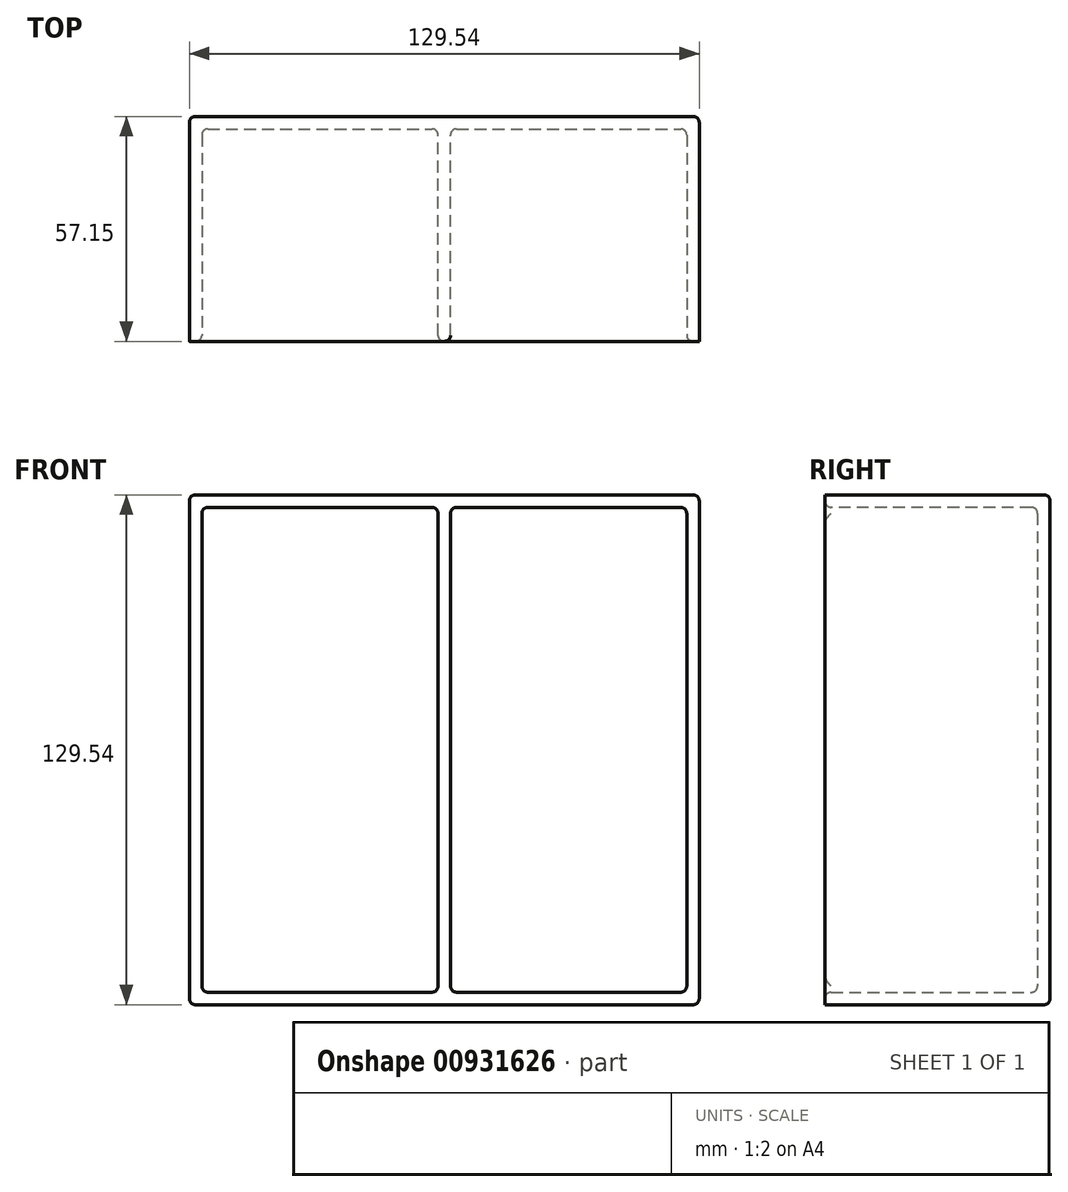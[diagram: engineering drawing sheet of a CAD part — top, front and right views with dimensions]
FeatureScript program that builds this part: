
annotation { "Feature Type Name" : "Feature", "Feature Type Description" : "" }
export const myFeature = defineFeature(function(context is Context, id is Id, definition is map)
    precondition{}
    {
        {
            var Q0;
            Q0=qCreatedBy(makeId("Front.planeOp"),FACE);
            var sketch = newSketch(context, id + "F0", { "sketchPlane" : qUnion([Q0])});
            skLineSegment(sketch, "E0.bottom", {"start": v(0, 0) * mm, "end": v(129.54, 0) * mm});
            skLineSegment(sketch, "E0.top", {"start": v(0, 129.54) * mm, "end": v(129.54, 129.54) * mm});
            skLineSegment(sketch, "E0.left", {"start": v(0, 0) * mm, "end": v(0, 129.54) * mm});
            skLineSegment(sketch, "E0.right", {"start": v(129.54, 0) * mm, "end": v(129.54, 129.54) * mm});
            skSolve(sketch);
        }
        {
            var Q0;
            Q0=makeQuery(id+"F0.imprint","IMPRINT",FACE,{"disambiguationData":[TD([[makeQuery(id+"F0.imprint","IMPRINT",EDGE,{"derivedFrom":sQuery(id+"F0.wireOp",EDGE,"E0.bottom")}),1.0]])]});
            extrude(context, id + "F1", {"entities" : qUnion([Q0]), "oppositeDirection" : true, "depth" : 57.15 * mm, "offsetDistance" : 25.4 * mm});
        }
        {
            var Q0;
            Q0=makeQuery(id+"F1.opExtrude","CAP_FACE",FACE,{"disambiguationData":[OSD([sQuery(id+"F0.wireOp",EDGE,"E0.bottom"),sQuery(id+"F0.wireOp",EDGE,"E0.top"),sQuery(id+"F0.wireOp",EDGE,"E0.left"),sQuery(id+"F0.wireOp",EDGE,"E0.right")])],"isStart":true});
            shell(context, id + "F2", {"entities" : qUnion([Q0]), "thickness" : 3.17 * mm});
        }
        {
            var Q0;
            Q0=makeQuery(id+"F2.opShell","OFFSET_EDGE",EDGE,{"disambiguationData":[OSD([sQuery(id+"F0.wireOp",EDGE,"E0.top"),sQuery(id+"F0.wireOp",EDGE,"E0.left")])]});
            var Q1;
            {var subQ0=sQuery(id+"F0.wireOp",EDGE,"E0.top");Q1=makeQuery(id+"F2.opShell","OFFSET_EDGE",EDGE,{"disambiguationData":[OSD([subQ0]),TDD([makeQuery(id+"F1.opExtrude","CAP_EDGE",EDGE,{"disambiguationData":[OSD([subQ0])],"isStart":false})])]});}
            var Q2;
            {var subQ0=sQuery(id+"F0.wireOp",EDGE,"E0.left");Q2=makeQuery(id+"F2.opShell","OFFSET_EDGE",EDGE,{"disambiguationData":[OSD([subQ0]),TDD([makeQuery(id+"F1.opExtrude","CAP_EDGE",EDGE,{"disambiguationData":[OSD([subQ0])],"isStart":false})])]});}
            var Q3;
            Q3=makeQuery(id+"F2.opShell","OFFSET_EDGE",EDGE,{"disambiguationData":[OSD([sQuery(id+"F0.wireOp",EDGE,"E0.bottom"),sQuery(id+"F0.wireOp",EDGE,"E0.left")])]});
            var Q4;
            {var subQ0=sQuery(id+"F0.wireOp",EDGE,"E0.bottom");Q4=makeQuery(id+"F2.opShell","OFFSET_EDGE",EDGE,{"disambiguationData":[OSD([subQ0]),TDD([makeQuery(id+"F1.opExtrude","CAP_EDGE",EDGE,{"disambiguationData":[OSD([subQ0])],"isStart":false})])]});}
            var Q5;
            {var subQ0=sQuery(id+"F0.wireOp",EDGE,"E0.right");Q5=makeQuery(id+"F2.opShell","OFFSET_EDGE",EDGE,{"disambiguationData":[OSD([subQ0]),TDD([makeQuery(id+"F1.opExtrude","CAP_EDGE",EDGE,{"disambiguationData":[OSD([subQ0])],"isStart":false})])]});}
            var Q6;
            Q6=makeQuery(id+"F2.opShell","OFFSET_EDGE",EDGE,{"disambiguationData":[OSD([sQuery(id+"F0.wireOp",EDGE,"E0.top"),sQuery(id+"F0.wireOp",EDGE,"E0.right")])]});
            var Q7;
            Q7=makeQuery(id+"F2.opShell","OFFSET_EDGE",EDGE,{"disambiguationData":[OSD([sQuery(id+"F0.wireOp",EDGE,"E0.bottom"),sQuery(id+"F0.wireOp",EDGE,"E0.right")])]});
            fillet(context, id + "F3", {"entities" : qUnion([Q0, Q1, Q2, Q3, Q4, Q5, Q6, Q7]), "radius" : 1.52 * mm, "tangentPropagation" : true, "allowEdgeOverflow" : false});
        }
        {
            var Q0;
            Q0=makeQuery(id+"F1.opExtrude","SWEPT_EDGE",EDGE,{"disambiguationData":[OSD([sQuery(id+"F0.wireOp",EDGE,"E0.bottom"),sQuery(id+"F0.wireOp",EDGE,"E0.right")])]});
            var Q1;
            Q1=makeQuery(id+"F1.opExtrude","CAP_EDGE",EDGE,{"disambiguationData":[OSD([sQuery(id+"F0.wireOp",EDGE,"E0.bottom")])],"isStart":false});
            var Q2;
            Q2=makeQuery(id+"F1.opExtrude","CAP_EDGE",EDGE,{"disambiguationData":[OSD([sQuery(id+"F0.wireOp",EDGE,"E0.right")])],"isStart":false});
            var Q3;
            Q3=makeQuery(id+"F1.opExtrude","SWEPT_EDGE",EDGE,{"disambiguationData":[OSD([sQuery(id+"F0.wireOp",EDGE,"E0.top"),sQuery(id+"F0.wireOp",EDGE,"E0.right")])]});
            var Q4;
            Q4=makeQuery(id+"F1.opExtrude","CAP_EDGE",EDGE,{"disambiguationData":[OSD([sQuery(id+"F0.wireOp",EDGE,"E0.top")])],"isStart":false});
            var Q5;
            Q5=makeQuery(id+"F1.opExtrude","SWEPT_EDGE",EDGE,{"disambiguationData":[OSD([sQuery(id+"F0.wireOp",EDGE,"E0.top"),sQuery(id+"F0.wireOp",EDGE,"E0.left")])]});
            var Q6;
            Q6=makeQuery(id+"F1.opExtrude","CAP_EDGE",EDGE,{"disambiguationData":[OSD([sQuery(id+"F0.wireOp",EDGE,"E0.left")])],"isStart":false});
            var Q7;
            Q7=makeQuery(id+"F1.opExtrude","SWEPT_EDGE",EDGE,{"disambiguationData":[OSD([sQuery(id+"F0.wireOp",EDGE,"E0.bottom"),sQuery(id+"F0.wireOp",EDGE,"E0.left")])]});
            fillet(context, id + "F4", {"entities" : qUnion([Q0, Q1, Q2, Q3, Q4, Q5, Q6, Q7]), "radius" : 1.52 * mm, "tangentPropagation" : true, "allowEdgeOverflow" : false});
        }
        {
            var Q0;
            Q0=makeQuery(id+"F2.opShell","OFFSET_FACE",FACE,{"disambiguationData":[OSD([sQuery(id+"F0.wireOp",EDGE,"E0.bottom"),sQuery(id+"F0.wireOp",EDGE,"E0.top"),sQuery(id+"F0.wireOp",EDGE,"E0.left"),sQuery(id+"F0.wireOp",EDGE,"E0.right")])]});
            var sketch = newSketch(context, id + "F5", { "sketchPlane" : qUnion([Q0])});
            skLineSegment(sketch, "E1.0", {"start": v(63.18, 126.37) * mm, "end": v(63.18, 3.17) * mm});
            skLineSegment(sketch, "E2.0", {"start": v(66.36, 126.37) * mm, "end": v(66.36, 3.17) * mm});
            skPoint(sketch, "E3.end.orphan", {"position": v(64.77, 3.17) * mm});
            skPoint(sketch, "E3.start.orphan", {"position": v(64.77, 126.37) * mm});
            skLineSegment(sketch, "E4", {"start": v(63.18, 126.37) * mm, "end": v(66.36, 126.37) * mm});
            skLineSegment(sketch, "E5", {"start": v(66.36, 3.17) * mm, "end": v(63.18, 3.17) * mm});
            skSolve(sketch);
        }
        {
            var Q0;
            Q0=makeQuery(id+"F5.imprint","IMPRINT",FACE,{"disambiguationData":[TD([[makeQuery(id+"F5.imprint","IMPRINT",EDGE,{"derivedFrom":sQuery(id+"F5.wireOp",EDGE,"E1.0")}),1.0]])]});
            extrude(context, id + "F6", {"entities" : qUnion([Q0]), "operationType" : NewBodyOperationType.ADD, "depth" : 53.97 * mm, "offsetDistance" : 25.4 * mm});
        }
        {
            var Q0;
            {var subQ1=sQuery(id+"F0.wireOp",EDGE,"E0.top");var subQ2=sQuery(id+"F5.wireOp",EDGE,"E1.0");Q0=makeQuery(id+"F6.boolean.opBoolean","SPLIT",EDGE,{"disambiguationData":[TD([makeQuery(id+"F6.opExtrude","SWEPT_FACE",FACE,{"disambiguationData":[OSD([subQ2])]})])],"derivedFrom":makeQuery(id+"F2.opShell","OFFSET_EDGE",EDGE,{"disambiguationData":[OSD([subQ1]),TDD([makeQuery(id+"F1.opExtrude","CAP_EDGE",EDGE,{"disambiguationData":[OSD([subQ1])],"isStart":true})])]})});}
            var Q1;
            Q1=makeQuery(id+"F6.opExtrude","CAP_EDGE",EDGE,{"disambiguationData":[OSD([sQuery(id+"F5.wireOp",EDGE,"E1.0")])],"isStart":false});
            var Q2;
            Q2=makeQuery(id+"F6.opExtrude","SWEPT_FACE",FACE,{"disambiguationData":[OSD([sQuery(id+"F5.wireOp",EDGE,"E1.0")])]});
            var Q3;
            {var subQ1=sQuery(id+"F0.wireOp",EDGE,"E0.top");var subQ2=sQuery(id+"F5.wireOp",EDGE,"E2.0");Q3=makeQuery(id+"F6.boolean.opBoolean","SPLIT",FACE,{"disambiguationData":[TD([makeQuery(id+"F6.opExtrude","SWEPT_FACE",FACE,{"disambiguationData":[OSD([subQ2])]})])],"derivedFrom":makeQuery(id+"F2.opShell","OFFSET_FACE",FACE,{"disambiguationData":[OSD([subQ1])]})});}
            var Q4;
            Q4=makeQuery(id+"F2.opShell","OFFSET_FACE",FACE,{"disambiguationData":[OSD([sQuery(id+"F0.wireOp",EDGE,"E0.right")])]});
            fillet(context, id + "F7", {"entities" : qUnion([Q0, Q1, Q2, Q3, Q4]), "radius" : 1.52 * mm, "tangentPropagation" : true, "allowEdgeOverflow" : false});
        }
    });
